# Revit family: Artek_Tables_Aalto Table square_Aalto Table square 81C
name_source: partatom
category: Furniture
revit_build: Autodesk Revit 2017 (Build: 20190508_0315(x64)
units: mm (PartAtom-declared; Revit-internal decimal feet)

## family parameters
Always vertical = Yes
Cut with Voids When Loaded = No
OmniClass Number = 23.40.20.14.17.11
OmniClass Title = Dining Room Tables
Room Calculation Point = No
Shared = No
Work Plane-Based = No

## types (5) — shared parameters
AssetType = Movable
BIMObjectName = Artek_Tables_Aalto Table square_Aalto Table square 81C
Brand = Artek
Category = Tables
ConvergoRefNr = 0190-2009-0017-FI
Designer = Alvar Aalto
IfcExportAs = IfcFurnishingElementType
IfcExportType = TABLE
Manufacturer = Artek
ManufacturerName = Artek
ManufacturerURL = https://www.artek.fi
Material = Wood
NBSDescription = Tables
NBSReference = 45-35-86/327
Name = Aalto Table square 81C
NominalDepth = 750 mm  [stored 2.46063 ft]
NominalHeight = 740 mm  [stored 2.42782 ft]
NominalLength = 750 mm  [stored 2.46063 ft]
Shape = Sculptured
Size = 750x740x750 mm
URL = https://www.artek.fi
Uniclass2 = Pr_40_50_21_21
Uniclass2015Description = Dining tables
Uniclass2015Reference = Pr_40_50_21_22
Version = 1
VersionDate = 03/11/2020
zero-valued in all types: Cost

## per-type parameters (varying)
| type | Color | MainColor | ModelNumber | TableMainMaterial | TableSecondaryMaterial |
| Aalto Table square 81C Birch | Natural birch | Natural birch | 28304581 | Natural Birch | Natural Birch |
| Aalto Table square 81C White laminate | Natural birch | Natural birch | 28304582 | White Laminate | Natural Birch |
| Aalto Table square 81C Black linoleum | Natural birch | Natural birch | 28304583 | Black Linoleum | Natural Birch |
| Aalto Table square 81C Linoleum black leg black | Black | Black | 28304584 | Black Linoleum | Black Linoleum |
| Aalto Table square 81C White HPL leg white | White | White | 28304585 | White Laminate | White Laminate |

note: column(s) folded — value = type name in every type: Model

note: [stored X ft] marks values corroborated as IEEE doubles in the binary element streams (Revit-internal decimal feet)

## geometry (parser evidence)
native form markers: Sweep x5
no freeform markers — native parametric forms only
